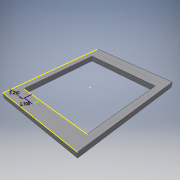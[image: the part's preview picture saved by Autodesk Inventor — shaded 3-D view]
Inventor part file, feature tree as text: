
AUTODESK INVENTOR PART (.ipt)
format: ipt  version: 2016 (Build 200138000, 138)  size: 114,176 bytes
history: native  units: in
note: dims shown in document units (in); Inventor stores cm internally (conversion verified against a paired STEP export)
features: extrude x3, sketch x3
ambient origin geometry x8: Origin, YZ Plane, XZ Plane, XY Plane, X Axis, Y Axis, Z Axis, Center Point
bodies: Solid1 (feature_tree)
feature tree (6):
  extrude  "Extrusion1"  Depth=16.0in
  extrude  "Extrusion2"  Depth=14.5in
  extrude  "Extrusion3"  Depth=1.0in TaperAngle=0.0deg
  sketch  "Sketch1"  dims[d0=20.0in d1=16.0in]
  sketch  "Sketch2"  dims[d2=1.0in d3=0.0in d4=14.5in]
  sketch  "Sketch3"  dims[d5=13.5in d6=1.0in d7=0.0in d8=1.5in d9=3.25in d10=2.0in d11=1.0in d12=0.0in]
